FCSTD DOCUMENT  (FreeCAD 1.0R39109 (Git))
Label: Assembly
License: All rights reserved
LicenseURL: https://en.wikipedia.org/wiki/All_rights_reserved
objects: App::FeaturePython×14, App::Link×5, Assembly::JointGroup×1, Assembly::AssemblyObject×1
EXTERNAL_REF file=HalfBridge_SiC.FCStd obj=Board_ed05
EXTERNAL_REF file=Rectifier.FCStd obj=Board_47f8
EXTERNAL_REF file=Backplane_DC.FCStd obj=Board_587c
EXTERNAL_REF file=Filter.FCStd obj=Board_ee73

FEATURE [App::Link] HalfBridge_SiC  label="HalfBridge_SiC1"
  LinkedObject = -> <external HalfBridge_SiC.FCStd>#Board_ed05
FEATURE [App::Link] HalfBridge_SiC001  label="HalfBridge_SiC2"
  LinkPlacement = pos=(-2.33e-14,5.4e-15,60.96) rot=(0,0,1;0rad)
  LinkedObject = -> <external HalfBridge_SiC.FCStd>#Board_ed05
  Placement = pos=(-2.33e-14,5.4e-15,60.96) rot=(0,0,1;0rad)
FEATURE [App::Link] Rectifier
  LinkPlacement = pos=(0.02,-1e-06,91.44) rot=(0,0,1;0rad)
  LinkedObject = -> <external Rectifier.FCStd>#Board_47f8
  Placement = pos=(0.02,-1e-06,91.44) rot=(0,0,1;0rad)
FEATURE [App::FeaturePython] GroundedJoint  # Assembly grounded joint (typed FeaturePython)
  ObjectToGround = -> HalfBridge_SiC
FEATURE [App::FeaturePython] Joint003  label="Parallel001"  # Assembly joint (typed FeaturePython)
  Activated = true
  AngleMax = 0
  AngleMin = 0
  Detach1 = false
  Detach2 = false
  Distance = 0
  Distance2 = 0
  EnableAngleMax = false
  EnableAngleMin = false
  EnableLengthMax = false
  EnableLengthMin = false
  JointType = 6 (Parallel)
  LengthMax = 0
  LengthMin = 0
  Placement1 = pos=(139.5,-40.5,0) rot=(1,0,0;1.5708rad)
  Placement2 = pos=(139.5,-40.5,0) rot=(1,0,0;1.5708rad)
  Reference1 = -> Assembly [HalfBridge_SiC.Board_Geoms_ed05.Pcb_ed05.Face1,HalfBridge_SiC.Board_Geoms_ed05.Pcb_ed05.Vertex3]
  Reference2 = -> Assembly [HalfBridge_SiC001.Board_Geoms_ed05.Pcb_ed05.Face1,HalfBridge_SiC001.Board_Geoms_ed05.Pcb_ed05.Vertex3]
FEATURE [App::Link] Backplane_DC
  LinkPlacement = pos=(101.6,-2e-06,92.078) rot=(0,1,0;1.5708rad)
  LinkedObject = -> <external Backplane_DC.FCStd>#Board_587c
  Placement = pos=(101.6,-2e-06,92.078) rot=(0,1,0;1.5708rad)
FEATURE [App::FeaturePython] Joint  label="Distance"  # Assembly joint (typed FeaturePython)
  Activated = true
  AngleMax = 0
  AngleMin = 0
  Detach1 = false
  Detach2 = false
  Distance = 0
  Distance2 = 0
  EnableAngleMax = false
  EnableAngleMin = false
  EnableLengthMax = false
  EnableLengthMin = false
  JointType = 5 (Distance)
  LengthMax = 0
  LengthMin = 0
  Placement1 = pos=(-1.42e-14,-3.5,2.35667) rot=(0.57735,0.57735,0.57735;4.18879rad)
  Placement2 = pos=(89.9794,-90.1131,-1.6) rot=(0,1,0;3.14159rad)
  Reference1 = -> Assembly [HalfBridge_SiC.Step_Models_ed05.Bot_ed05.J13_1_cfcac89c0bd5_2__ln_001.Face4,HalfBridge_SiC.Step_Models_ed05.Bot_ed05.J13_1_cfcac89c0bd5_2__ln_001.Vertex4]
  Reference2 = -> Assembly [Backplane_DC.Board_Geoms_587c.Pcb_587c.Face27,Backplane_DC.Board_Geoms_587c.Pcb_587c.Face27]
FEATURE [App::FeaturePython] Joint004  label="Cylindrical"  # Assembly joint (typed FeaturePython)
  Activated = true
  AngleMax = 0
  AngleMin = 0
  Detach1 = false
  Detach2 = false
  Distance = 0
  Distance2 = 0
  EnableAngleMax = false
  EnableAngleMin = false
  EnableLengthMax = false
  EnableLengthMin = false
  JointType = 2 (Cylindrical)
  LengthMax = 0
  LengthMin = 0
  Placement1 = pos=(0,-3.13,1.98) rot=(0.57735,0.57735,-0.57735;2.0944rad)
  Placement2 = pos=(135.658,-116.2,-0.8) rot=(0,0,1;0rad)
  Reference1 = -> Assembly [HalfBridge_SiC.Step_Models_ed05.Bot_ed05.J13_1_cfcac89c0bd5_2__ln_001.Face2,HalfBridge_SiC.Step_Models_ed05.Bot_ed05.J13_1_cfcac89c0bd5_2__ln_001.Edge3]
  Reference2 = -> Assembly [Backplane_DC.Board_Geoms_587c.Pcb_587c.Face11,Backplane_DC.Board_Geoms_587c.Pcb_587c.Face11]
FEATURE [App::FeaturePython] Joint005  label="Parallel"  # Assembly joint (typed FeaturePython)
  Activated = true
  AngleMax = 0
  AngleMin = 0
  Detach1 = false
  Detach2 = false
  Distance = 0
  Distance2 = 0
  EnableAngleMax = false
  EnableAngleMin = false
  EnableLengthMax = false
  EnableLengthMin = false
  JointType = 6 (Parallel)
  LengthMax = 0
  LengthMin = 0
  Placement1 = pos=(139.5,-140.5,-1.6) rot=(0,0.707107,0.707107;3.14159rad)
  Placement2 = pos=(140,-140,-1.6) rot=(0,0.707107,0.707107;3.14159rad)
  Reference1 = -> Assembly [HalfBridge_SiC.Board_Geoms_ed05.Pcb_ed05.Face4,HalfBridge_SiC.Board_Geoms_ed05.Pcb_ed05.Vertex8]
  Reference2 = -> Assembly [Backplane_DC.Board_Geoms_587c.Pcb_587c.Face4,Backplane_DC.Board_Geoms_587c.Pcb_587c.Vertex8]
FEATURE [App::FeaturePython] Joint006  label="Distance001"  # Assembly joint (typed FeaturePython)
  Activated = true
  AngleMax = 0
  AngleMin = 0
  Detach1 = false
  Detach2 = false
  Distance = 0
  Distance2 = 0
  EnableAngleMax = false
  EnableAngleMin = false
  EnableLengthMax = false
  EnableLengthMin = false
  JointType = 5 (Distance)
  LengthMax = 0
  LengthMin = 0
  Placement1 = pos=(-1.42e-14,-3.5,2.35667) rot=(0.57735,0.57735,0.57735;4.18879rad)
  Placement2 = pos=(89.9794,-90.1131,-1.6) rot=(0,1,0;3.14159rad)
  Reference1 = -> Assembly [HalfBridge_SiC001.Step_Models_ed05.Bot_ed05.J13_1_cfcac89c0bd5_2__ln_001.Face4,HalfBridge_SiC001.Step_Models_ed05.Bot_ed05.J13_1_cfcac89c0bd5_2__ln_001.Vertex4]
  Reference2 = -> Assembly [Backplane_DC.Board_Geoms_587c.Pcb_587c.Face27,Backplane_DC.Board_Geoms_587c.Pcb_587c.Vertex28]
FEATURE [App::FeaturePython] Joint007  label="Cylindrical001"  # Assembly joint (typed FeaturePython)
  Activated = true
  AngleMax = 0
  AngleMin = 0
  Detach1 = false
  Detach2 = false
  Distance = 0
  Distance2 = 0
  EnableAngleMax = false
  EnableAngleMin = false
  EnableLengthMax = false
  EnableLengthMin = false
  JointType = 2 (Cylindrical)
  LengthMax = 0
  LengthMin = 0
  Placement1 = pos=(0,3.13,1.98) rot=(0.57735,0.57735,-0.57735;2.0944rad)
  Placement2 = pos=(74.698,-116.2,-0.8) rot=(0,0,1;0rad)
  Reference1 = -> Assembly [HalfBridge_SiC001.Step_Models_ed05.Bot_ed05.J13_1_cfcac89c0bd5_2__ln_001.Face2,HalfBridge_SiC001.Step_Models_ed05.Bot_ed05.J13_1_cfcac89c0bd5_2__ln_001.Edge1]
  Reference2 = -> Assembly [Backplane_DC.Board_Geoms_587c.Pcb_587c.Face15,Backplane_DC.Board_Geoms_587c.Pcb_587c.Face15]
FEATURE [App::FeaturePython] Joint008  label="Parallel002"  # Assembly joint (typed FeaturePython)
  Activated = true
  AngleMax = 0
  AngleMin = 0
  Detach1 = false
  Detach2 = false
  Distance = 0
  Distance2 = 0
  EnableAngleMax = false
  EnableAngleMin = false
  EnableLengthMax = false
  EnableLengthMin = false
  JointType = 6 (Parallel)
  LengthMax = 0
  LengthMin = 0
  Placement1 = pos=(139.5,-140.5,-1.6) rot=(0,0.707107,0.707107;3.14159rad)
  Placement2 = pos=(90,-140,-0.8) rot=(0,0.707107,0.707107;3.14159rad)
  Reference1 = -> Assembly [HalfBridge_SiC001.Board_Geoms_ed05.Pcb_ed05.Face4,HalfBridge_SiC001.Board_Geoms_ed05.Pcb_ed05.Vertex8]
  Reference2 = -> Assembly [Backplane_DC.Board_Geoms_587c.Pcb_587c.Face4,Backplane_DC.Board_Geoms_587c.Pcb_587c.Face4]
FEATURE [App::FeaturePython] Joint009  label="Distance002"  # Assembly joint (typed FeaturePython)
  Activated = true
  AngleMax = 0
  AngleMin = 0
  Detach1 = false
  Detach2 = false
  Distance = 0
  Distance2 = 0
  EnableAngleMax = false
  EnableAngleMin = false
  EnableLengthMax = false
  EnableLengthMin = false
  JointType = 5 (Distance)
  LengthMax = 0
  LengthMin = 0
  Placement1 = pos=(-1.42e-14,-3.5,2.35667) rot=(0.57735,0.57735,0.57735;4.18879rad)
  Placement2 = pos=(89.9794,-90.1131,-1.6) rot=(0,1,0;3.14159rad)
  Reference1 = -> Assembly [Rectifier.Step_Models_47f8.Bot_47f8.J3_1_837fcd1c15ac_2__ln_001.Face4,Rectifier.Step_Models_47f8.Bot_47f8.J3_1_837fcd1c15ac_2__ln_001.Vertex7]
  Reference2 = -> Assembly [Backplane_DC.Board_Geoms_587c.Pcb_587c.Face27,Backplane_DC.Board_Geoms_587c.Pcb_587c.Vertex32]
FEATURE [App::FeaturePython] Joint010  label="Cylindrical002"  # Assembly joint (typed FeaturePython)
  Activated = true
  AngleMax = 0
  AngleMin = 0
  Detach1 = false
  Detach2 = false
  Distance = 0
  Distance2 = 0
  EnableAngleMax = false
  EnableAngleMin = false
  EnableLengthMax = false
  EnableLengthMin = false
  JointType = 2 (Cylindrical)
  LengthMax = 0
  LengthMin = 0
  Placement1 = pos=(0,-3.13,1.98) rot=(0.57735,0.57735,-0.57735;2.0944rad)
  Placement2 = pos=(44.218,-75.56,-0.8) rot=(0,0,1;0rad)
  Reference1 = -> Assembly [Rectifier.Step_Models_47f8.Bot_47f8.J3_1_837fcd1c15ac_2__ln_.Face2,Rectifier.Step_Models_47f8.Bot_47f8.J3_1_837fcd1c15ac_2__ln_.Edge3]
  Reference2 = -> Assembly [Backplane_DC.Board_Geoms_587c.Pcb_587c.Face23,Backplane_DC.Board_Geoms_587c.Pcb_587c.Face23]
FEATURE [App::FeaturePython] Joint011  label="Parallel003"  # Assembly joint (typed FeaturePython)
  Activated = true
  AngleMax = 0
  AngleMin = 0
  Detach1 = false
  Detach2 = false
  Distance = 0
  Distance2 = 0
  EnableAngleMax = false
  EnableAngleMin = false
  EnableLengthMax = false
  EnableLengthMin = false
  JointType = 6 (Parallel)
  LengthMax = 0
  LengthMin = 0
  Placement1 = pos=(153.67,-129.248,0) rot=(0,0.707107,0.707107;3.14159rad)
  Placement2 = pos=(40,-140,0) rot=(0,0.707107,0.707107;3.14159rad)
  Reference1 = -> Assembly [Rectifier.Board_Geoms_47f8.Pcb_47f8.Face4,Rectifier.Board_Geoms_47f8.Pcb_47f8.Vertex7]
  Reference2 = -> Assembly [Backplane_DC.Board_Geoms_587c.Pcb_587c.Face4,Backplane_DC.Board_Geoms_587c.Pcb_587c.Vertex5]
FEATURE [App::Link] Filter
  LinkPlacement = pos=(101.6,88.8,-7.922) rot=(1,0,0;1.5708rad)
  LinkedObject = -> <external Filter.FCStd>#Board_ee73
  Placement = pos=(101.6,88.8,-7.922) rot=(1,0,0;1.5708rad)
FEATURE [App::FeaturePython] Joint012  label="Distance003"  # Assembly joint (typed FeaturePython)
  Activated = true
  AngleMax = 0
  AngleMin = 0
  Detach1 = false
  Detach2 = false
  Distance = 0
  Distance2 = 0
  EnableAngleMax = false
  EnableAngleMin = false
  EnableLengthMax = false
  EnableLengthMin = false
  JointType = 5 (Distance)
  LengthMax = 0
  LengthMin = 0
  Placement1 = pos=(-1.42e-14,3.5,2.35667) rot=(0.57735,0.57735,0.57735;4.18879rad)
  Placement2 = pos=(89.9794,-90.1131,0) rot=(0,1,0;3.14159rad)
  Reference1 = -> Assembly [Filter.Step_Models_ee73.Bot_ee73.J2_1_276a3e213de9_2__ln_.Face5,Filter.Step_Models_ee73.Bot_ee73.J2_1_276a3e213de9_2__ln_.Vertex1]
  Reference2 = -> Assembly [Backplane_DC.Board_Geoms_587c.Pcb_587c.Face26,Backplane_DC.Board_Geoms_587c.Pcb_587c.Edge21]
FEATURE [App::FeaturePython] Joint013  label="Cylindrical003"  # Assembly joint (typed FeaturePython)
  Activated = true
  AngleMax = 0
  AngleMin = 0
  Detach1 = false
  Detach2 = false
  Distance = 0
  Distance2 = 0
  EnableAngleMax = false
  EnableAngleMin = false
  EnableLengthMax = false
  EnableLengthMin = false
  JointType = 2 (Cylindrical)
  LengthMax = 0
  LengthMin = 0
  Placement1 = pos=(128.038,-47.62,-0.8) rot=(0,0,1;0rad)
  Placement2 = pos=(1.8e-15,-3.13,1.98) rot=(0.57735,0.57735,-0.57735;2.0944rad)
  Reference1 = -> Assembly [Backplane_DC.Board_Geoms_587c.Pcb_587c.Face21,Backplane_DC.Board_Geoms_587c.Pcb_587c.Face21]
  Reference2 = -> Assembly [Filter.Step_Models_ee73.Bot_ee73.Shape002.Face2,Filter.Step_Models_ee73.Bot_ee73.Shape002.Edge3]
FEATURE [App::FeaturePython] Joint014  label="Parallel004"  # Assembly joint (typed FeaturePython)
  Activated = true
  AngleMax = 0
  AngleMin = 0
  Detach1 = false
  Detach2 = false
  Distance = 0
  Distance2 = 0
  EnableAngleMax = false
  EnableAngleMin = false
  EnableLengthMax = false
  EnableLengthMin = false
  JointType = 6 (Parallel)
  LengthMax = 0
  LengthMin = 0
  Placement1 = pos=(140,-40,0) rot=(0.57735,-0.57735,-0.57735;2.0944rad)
  Placement2 = pos=(40,-160,0) rot=(0,0.707107,0.707107;3.14159rad)
  Reference1 = -> Assembly [Backplane_DC.Board_Geoms_587c.Pcb_587c.Face3,Backplane_DC.Board_Geoms_587c.Pcb_587c.Vertex3]
  Reference2 = -> Assembly [Filter.Board_Geoms_ee73.Pcb_ee73.Face4,Filter.Board_Geoms_ee73.Pcb_ee73.Vertex5]
FEATURE [Assembly::JointGroup] Joints
  Group = -> [GroundedJoint,Joint003,Joint,Joint004,Joint005,Joint006,Joint007,Joint008,Joint009,Joint010,Joint011,Joint012,Joint013,Joint014]
FEATURE [Assembly::AssemblyObject] Assembly
  Group = -> [Joints,HalfBridge_SiC,HalfBridge_SiC001,Rectifier,GroundedJoint,Joint003,Backplane_DC,Joint,Joint004,Joint005,Joint006,Joint007,Joint008,Joint009,Joint010,Joint011,Filter,Joint012,Joint013,Joint014]
  Origin = -> Origin
  Type = Assembly

RESOLVED EXTERNAL PARTS (link-assembly join: the EXTERNAL_REF files above that resolve inside this repo's crawl, each included once):
---- part HalfBridge_SiC.FCStd = doc fcstd_651f331eab62 ----
FCSTD DOCUMENT  (FreeCAD 1.0R39109 (Git))
Label: HalfBridge_SiC
License: All rights reserved
LicenseURL: https://en.wikipedia.org/wiki/All_rights_reserved
objects: App::Link×105, Part::Feature×46, App::Part×15, PartDesign::CoordinateSystem×1, Sketcher::SketchObject×1
note: 49 computed .brp shape members not serialized (recipe doc carries the construction recipe); baked Part::Feature solids carry a one-line shape summary decoded from their .brp

FEATURE [PartDesign::CoordinateSystem] Local_CS_ed05
  AttacherType = Attacher::AttachEngine3D
  MapMode = 2
FEATURE [Part::Feature] Pcb_ed05
  Placement = pos=(-39.5,140.5,0) rot=(0,0,1;0rad)
  shape: bbox 100 x 100 x 1.6 mm, 113 faces (baked)
FEATURE [Sketcher::SketchObject] PCB_Sketch_ed05
  ArcFitTolerance = 1e-06
  FullyConstrained = false
  MakeInternals = false
  sketch-geometry (28):
    g0: LineSegment StartX=17.542 StartY=39.29 StartZ=0 EndX=18.542 EndY=39.29 EndZ=0
    g1: LineSegment StartX=18.542 StartY=39.29 StartZ=0 EndX=18.542 EndY=29.29 EndZ=0
    g2: LineSegment StartX=18.542 StartY=29.29 StartZ=0 EndX=17.542 EndY=29.29 EndZ=0
    g3: LineSegment StartX=17.542 StartY=29.29 StartZ=0 EndX=17.542 EndY=39.29 EndZ=0
    g4: LineSegment StartX=36.399 StartY=40.662 StartZ=0 EndX=45.383 EndY=40.662 EndZ=0
    g5: LineSegment StartX=45.383 StartY=40.662 StartZ=0 EndX=45.383 EndY=39.662 EndZ=0
    g6: LineSegment StartX=45.383 StartY=39.662 StartZ=0 EndX=36.399 EndY=39.662 EndZ=0
    g7: LineSegment StartX=36.399 StartY=39.662 StartZ=0 EndX=36.399 EndY=40.662 EndZ=0
    g8: LineSegment StartX=47.768 StartY=91.487 StartZ=0 EndX=48.514 EndY=91.487 EndZ=0
    g9: LineSegment StartX=48.514 StartY=91.487 StartZ=0 EndX=48.514 EndY=59.389 EndZ=0
    g10: LineSegment StartX=48.514 StartY=59.389 StartZ=0 EndX=47.768 EndY=59.389 EndZ=0
    g11: LineSegment StartX=47.768 StartY=59.389 StartZ=0 EndX=47.768 EndY=91.487 EndZ=0
    g12: LineSegment StartX=17.968 StartY=23.7 StartZ=0 EndX=74.68 EndY=23.7 EndZ=0
    g13: LineSegment StartX=74.68 StartY=23.7 StartZ=0 EndX=74.68 EndY=22.7 EndZ=0
    g14: LineSegment StartX=74.68 StartY=22.7 StartZ=0 EndX=17.968 EndY=22.7 EndZ=0
    g15: LineSegment StartX=17.968 StartY=22.7 StartZ=0 EndX=17.968 EndY=23.7 EndZ=0
    g16: LineSegment StartX=0 StartY=100 StartZ=0 EndX=100 EndY=100 EndZ=0
    g17: LineSegment StartX=100 StartY=100 StartZ=0 EndX=100 EndY=0 EndZ=0
    g18: LineSegment StartX=100 StartY=0 StartZ=0 EndX=0 EndY=0 EndZ=0
    g19: LineSegment StartX=0 StartY=0 StartZ=0 EndX=0 EndY=100 EndZ=0
    g20: LineSegment StartX=18.05 StartY=15.208 StartZ=0 EndX=19.05 EndY=15.208 EndZ=0
    g21: LineSegment StartX=19.05 StartY=15.208 StartZ=0 EndX=19.05 EndY=8.7 EndZ=0
    g22: LineSegment StartX=19.05 StartY=8.7 StartZ=0 EndX=18.05 EndY=8.7 EndZ=0
    g23: LineSegment StartX=18.05 StartY=8.7 StartZ=0 EndX=18.05 EndY=15.208 EndZ=0
    g24: LineSegment StartX=15.764 StartY=29.4 StartZ=0 EndX=16.764 EndY=29.4 EndZ=0
    g25: LineSegment StartX=16.764 StartY=29.4 StartZ=0 EndX=16.764 EndY=16.9 EndZ=0
    g26: LineSegment StartX=16.764 StartY=16.9 StartZ=0 EndX=15.764 EndY=16.9 EndZ=0
    g27: LineSegment StartX=15.764 StartY=16.9 StartZ=0 EndX=15.764 EndY=29.4 EndZ=0
  constraints (28):
    c: Coincident(g18,g19)
    c: Coincident(g16,g19)
    c: Coincident(g26,g27)
    c: Coincident(g24,g27)
    c: Coincident(g25,g26)
    c: Coincident(g24,g25)
    c: Coincident(g2,g3)
    c: Coincident(g0,g3)
    c: Coincident(g14,g15)
    c: Coincident(g12,g15)
    c: Coincident(g22,g23)
    c: Coincident(g20,g23)
    c: Coincident(g1,g2)
    c: Coincident(g0,g1)
    c: Coincident(g21,g22)
    c: Coincident(g20,g21)
    c: Coincident(g6,g7)
    c: Coincident(g4,g7)
    c: Coincident(g5,g6)
    c: Coincident(g4,g5)
    c: Coincident(g10,g11)
    c: Coincident(g8,g11)
    c: Coincident(g9,g10)
    c: Coincident(g8,g9)
    c: Coincident(g13,g14)
    c: Coincident(g12,g13)
    c: Coincident(g17,g18)
    c: Coincident(g16,g17)
FEATURE [App::Part] Board_Geoms_ed05
  Group = -> [Pcb_ed05,PCB_Sketch_ed05]
  Origin = -> Origin
FEATURE [Part::Feature] Shape  label="U5_SOIC-16W_7.5x10.3mm_P1.27mm_noPin12_13_606f1c37d418"
  Placement = pos=(18,23.3,0) rot=(0,0,1;0rad)
  shape: bbox 10.3 x 10.3 x 2.75 mm, 256 faces (baked)
FEATURE [Part::Feature] Shape001  label="D6_D_SOD_123_86f777a7cf57"
  Placement = pos=(31.3,17.35,0) rot=(0,0,-1;1.5708rad)
  shape: bbox 1.6 x 3.8 x 1.25 mm, 67 faces (baked)
FEATURE [Part::Feature] Shape002  label="R9_R_0603_1608Metric_fe9d9f34c5f9"
  Placement = pos=(9.9875,27.2,0) rot=(0,0,1;0rad)
  shape: bbox 1.6 x 0.8 x 0.45 mm, 26 faces (baked)
FEATURE [App::Link] D6_D_SOD_123_86f777a7cf57_ln_  label="D5_D_SOD_123_75c73be4f775"
  LinkPlacement = pos=(31.3,29.9,0) rot=(0,0,1;1.5708rad)
  LinkedObject = -> Shape001
  Placement = pos=(31.3,29.9,0) rot=(0,0,1;1.5708rad)
FEATURE [Part::Feature] Shape003  label="C15_C_0603_1608Metric_09ddd0478757"
  Placement = pos=(13.5,16.1,0) rot=(0,0,-1;1.5708rad)
  shape: bbox 0.8 x 1.6 x 0.8 mm, 28 faces (baked)
FEATURE [App::Link] C15_C_0603_1608Metric_09ddd0478757_ln_  label="C33_C_0603_1608Metric_74bc470caa33"
  LinkPlacement = pos=(9.3,80.8715,0) rot=(0,0,1;1.5708rad)
  LinkedObject = -> Shape003
  Placement = pos=(9.3,80.8715,0) rot=(0,0,1;1.5708rad)
FEATURE [Part::Feature] Shape004  label="D3_LED_0603_1608Metric_70bb5031e2ff"
  Placement = pos=(4.7,31.775,0) rot=(0,0,-1;1.5708rad)
  shape: bbox 0.8 x 1.6 x 1.1 mm, 50 faces (baked)
FEATURE [Part::Feature] Shape005  label="C38_C_0805_2012Metric_74cbd35bff10"
  Placement = pos=(6.655,73.284,0) rot=(0,0,1;0rad)
  shape: bbox 2 x 1.25 x 1.25 mm, 28 faces (baked)
FEATURE [App::Link] R9_R_0603_1608Metric_fe9d9f34c5f9_ln_  label="R33_R_0603_1608Metric_ea8747869db3"
  LinkPlacement = pos=(22.7,83.4115,0) rot=(0,0,1;1.5708rad)
  LinkedObject = -> Shape002
  Placement = pos=(22.7,83.4115,0) rot=(0,0,1;1.5708rad)
FEATURE [App::Link] C15_C_0603_1608Metric_09ddd0478757_ln_001  label="C22_C_0603_1608Metric_3b7886544036"
  LinkPlacement = pos=(25.65,28.3,0) rot=(0,0,1;0rad)
  LinkedObject = -> Shape003
  Placement = pos=(25.65,28.3,0) rot=(0,0,1;0rad)
FEATURE [Part::Feature] Part__Feature  label="CAS_c_12B"
  Placement = pos=(0,-2.4,-3e-16) rot=(0,0,1;0rad)
  shape: bbox 5.4 x 2.5 x 4.2 mm, 71 faces (baked)
FEATURE [Part::Feature] Part__Feature001  label="1 pole_s"
  Placement = pos=(0.3,-0.6,-3e-16) rot=(0,0,1;0rad)
  shape: bbox 0.6 x 0.6 x 0.7 mm, 14 faces (baked)
FEATURE [App::Part] CAS_120B1  label="SW1_CAS-120B1_eba1f44a47b7[2]"
  Group = -> [Part__Feature,Part__Feature001]
  Origin = -> Origin008
  Placement = pos=(29.242,83.058,2.5) rot=(0.57735,-0.57735,-0.57735;2.0944rad)
FEATURE [App::Link] R9_R_0603_1608Metric_fe9d9f34c5f9_ln_001  label="R14_R_0603_1608Metric_f9b5c031c635"
  LinkPlacement = pos=(28.1,36.5,0) rot=(0,0,1;1.5708rad)
  LinkedObject = -> Shape002
  Placement = pos=(28.1,36.5,0) rot=(0,0,1;1.5708rad)
FEATURE [App::Link] R9_R_0603_1608Metric_fe9d9f34c5f9_ln_002  label="R8_R_0603_1608Metric_fcb6b5fbbfd0"
  LinkPlacement = pos=(10,28.7,0) rot=(0,0,1;0rad)
  LinkedObject = -> Shape002
  Placement = pos=(10,28.7,0) rot=(0,0,1;0rad)
FEATURE [App::Link] C15_C_0603_1608Metric_09ddd0478757_ln_002  label="C45_C_0603_1608Metric_6c9f5762c5a1"
  LinkPlacement = pos=(36.9,16.256,0) rot=(0,0,1;1.5708rad)
  LinkedObject = -> Shape003
  Placement = pos=(36.9,16.256,0) rot=(0,0,1;1.5708rad)
FEATURE [App::Link] C38_C_0805_2012Metric_74cbd35bff10_ln_  label="C24_C_0805_2012Metric_4c91d95a9eef"
  LinkPlacement = pos=(25.7,8.7,0) rot=(0,0,1;3.14159rad)
  LinkedObject = -> Shape005
  Placement = pos=(25.7,8.7,0) rot=(0,0,1;3.14159rad)
FEATURE [Part::Feature] Shape006  label="U10_SOT_23_6_8cf1dc40b667"
  Placement = pos=(21.85,68.3115,0) rot=(0,0,1;3.14159rad)
  shape: bbox 2.8 x 2.9 x 1.55 mm, 124 faces (baked)
FEATURE [App::Link] C15_C_0603_1608Metric_09ddd0478757_ln_003  label="C21_C_0603_1608Metric_d16c1e161e8d"
  LinkPlacement = pos=(25.62,18.5,0) rot=(0,0,1;3.14159rad)
  LinkedObject = -> Shape003
  Placement = pos=(25.62,18.5,0) rot=(0,0,1;3.14159rad)
FEATURE [App::Link] C15_C_0603_1608Metric_09ddd0478757_ln_004  label="C42_C_0603_1608Metric_20bf4b114d9d"
  LinkPlacement = pos=(25.1,68.1115,0) rot=(0,0,1;1.5708rad)
  LinkedObject = -> Shape003
  Placement = pos=(25.1,68.1115,0) rot=(0,0,1;1.5708rad)
FEATURE [App::Link] C38_C_0805_2012Metric_74cbd35bff10_ln_001  label="C18_C_0805_2012Metric_4df3bd6c3c50"
  LinkPlacement = pos=(25.7,33.1,0) rot=(0,0,1;3.14159rad)
  LinkedObject = -> Shape005
  Placement = pos=(25.7,33.1,0) rot=(0,0,1;3.14159rad)
FEATURE [App::Link] U10_SOT_23_6_8cf1dc40b667_ln_  label="U11_SOT_23_6_c211cb7acc4a"
  LinkPlacement = pos=(21.85,58.1515,0) rot=(0,0,1;3.14159rad)
  LinkedObject = -> Shape006
  Placement = pos=(21.85,58.1515,0) rot=(0,0,1;3.14159rad)
FEATURE [App::Link] R9_R_0603_1608Metric_fe9d9f34c5f9_ln_003  label="R15_R_0603_1608Metric_55e85660f00f"
  LinkPlacement = pos=(22.6,36.1,0) rot=(0,0,-1;1.5708rad)
  LinkedObject = -> Shape002
  Placement = pos=(22.6,36.1,0) rot=(0,0,-1;1.5708rad)
FEATURE [Part::Feature] Shape007  label="R21_R_0805_2012Metric_4eff570911b6"
  Placement = pos=(34.3,28.2,0) rot=(0,0,1;0rad)
  shape: bbox 2 x 1.2 x 0.45 mm, 26 faces (baked)
FEATURE [App::Link] C15_C_0603_1608Metric_09ddd0478757_ln_005  label="C34_C_0603_1608Metric_836b7f75df63"
  LinkPlacement = pos=(9.5,60.3715,0) rot=(0,0,1;1.5708rad)
  LinkedObject = -> Shape003
  Placement = pos=(9.5,60.3715,0) rot=(0,0,1;1.5708rad)
FEATURE [App::Link] C38_C_0805_2012Metric_74cbd35bff10_ln_002  label="C39_C_0805_2012Metric_4739b33e3560"
  LinkPlacement = pos=(6.655,83.9115,0) rot=(0,0,1;0rad)
  LinkedObject = -> Shape005
  Placement = pos=(6.655,83.9115,0) rot=(0,0,1;0rad)
FEATURE [App::Link] R9_R_0603_1608Metric_fe9d9f34c5f9_ln_004  label="R16_R_0603_1608Metric_5e29ad9bbd6c"
  LinkPlacement = pos=(29.7,13.3,0) rot=(0,0,-1;1.5708rad)
  LinkedObject = -> Shape002
  Placement = pos=(29.7,13.3,0) rot=(0,0,-1;1.5708rad)
FEATURE [App::Link] C15_C_0603_1608Metric_09ddd0478757_ln_006  label="C6_C_0603_1608Metric_47ec0beeeb7c"
  LinkPlacement = pos=(36.576,85.598,0) rot=(0,0,1;0rad)
  LinkedObject = -> Shape003
  Placement = pos=(36.576,85.598,0) rot=(0,0,1;0rad)
FEATURE [App::Link] D3_LED_0603_1608Metric_70bb5031e2ff_ln_  label="D1_LED_0603_1608Metric_117d22e4d741"
  LinkPlacement = pos=(3.1,9.525,0) rot=(0,0,1;1.5708rad)
  LinkedObject = -> Shape004
  Placement = pos=(3.1,9.525,0) rot=(0,0,1;1.5708rad)
FEATURE [Part::Feature] Shape008  label="U3_SOT_23_5_e32904241429"
  Placement = pos=(34.37,62.7015,0) rot=(0,0,1;0rad)
  shape: bbox 2.8 x 2.9 x 1.55 mm, 109 faces (baked)
FEATURE [App::Link] C38_C_0805_2012Metric_74cbd35bff10_ln_003  label="C35_C_0805_2012Metric_12818f10c88b"
  LinkPlacement = pos=(7.5,67.9115,0) rot=(0,0,1;3.14159rad)
  LinkedObject = -> Shape005
  Placement = pos=(7.5,67.9115,0) rot=(0,0,1;3.14159rad)
FEATURE [Part::Feature] Shape009  label="U7_SOT_23_ed8fd63cd947"
  Placement = pos=(25.3625,36.5,0) rot=(0,0,1;3.14159rad)
  shape: bbox 2.5 x 3 x 1.2 mm, 76 faces (baked)
FEATURE [Part::Feature] Shape010  label="C5_C_2220_5750Metric_40789e461117"
  Placement = pos=(71.498,23.622,0) rot=(0,0,-1;1.5708rad)
  shape: bbox 5 x 5.7 x 2.9 mm, 28 faces (baked)
FEATURE [App::Link] R9_R_0603_1608Metric_fe9d9f34c5f9_ln_005  label="R29_R_0603_1608Metric_c415b56a8a35"
  LinkPlacement = pos=(13.655,63.4115,0) rot=(0,0,1;1.5708rad)
  LinkedObject = -> Shape002
  Placement = pos=(13.655,63.4115,0) rot=(0,0,1;1.5708rad)
FEATURE [App::Link] R9_R_0603_1608Metric_fe9d9f34c5f9_ln_006  label="R27_R_0603_1608Metric_6ecdd8c441b3"
  LinkPlacement = pos=(13.3,73.9115,0) rot=(0,0,1;1.5708rad)
  LinkedObject = -> Shape002
  Placement = pos=(13.3,73.9115,0) rot=(0,0,1;1.5708rad)
FEATURE [App::Link] R9_R_0603_1608Metric_fe9d9f34c5f9_ln_007  label="R30_R_0603_1608Metric_3d9fcfb98980"
  LinkPlacement = pos=(18.7,78.4115,0) rot=(0,0,1;1.5708rad)
  LinkedObject = -> Shape002
  Placement = pos=(18.7,78.4115,0) rot=(0,0,1;1.5708rad)
FEATURE [App::Link] C15_C_0603_1608Metric_09ddd0478757_ln_007  label="C41_C_0603_1608Metric_8a3fc6cb6ce4"
  LinkPlacement = pos=(25.1,78.4115,0) rot=(0,0,1;1.5708rad)
  LinkedObject = -> Shape003
  Placement = pos=(25.1,78.4115,0) rot=(0,0,1;1.5708rad)
FEATURE [App::Link] C5_C_2220_5750Metric_40789e461117_ln_  label="C3_C_2220_5750Metric_0b14797a19db"
  LinkPlacement = pos=(59.498,23.622,0) rot=(0,0,-1;1.5708rad)
  LinkedObject = -> Shape010
  Placement = pos=(59.498,23.622,0) rot=(0,0,-1;1.5708rad)
FEATURE [App::Link] R21_R_0805_2012Metric_4eff570911b6_ln_  label="R19_R_0805_2012Metric_5467f9f4486e"
  LinkPlacement = pos=(34.3,32.2,0) rot=(0,0,1;0rad)
  LinkedObject = -> Shape007
  Placement = pos=(34.3,32.2,0) rot=(0,0,1;0rad)
FEATURE [App::Link] C15_C_0603_1608Metric_09ddd0478757_ln_008  label="C43_C_0603_1608Metric_b35c248b52c4"
  LinkPlacement = pos=(25.1,58.1115,0) rot=(0,0,1;1.5708rad)
  LinkedObject = -> Shape003
  Placement = pos=(25.1,58.1115,0) rot=(0,0,1;1.5708rad)
FEATURE [App::Link] R21_R_0805_2012Metric_4eff570911b6_ln_001  label="R3_R_0805_2012Metric_ab16afa742b3"
  LinkPlacement = pos=(44.564,16.278,0) rot=(0,0,1;1.5708rad)
  LinkedObject = -> Shape007
  Placement = pos=(44.564,16.278,0) rot=(0,0,1;1.5708rad)
FEATURE [App::Link] R21_R_0805_2012Metric_4eff570911b6_ln_002  label="R10_R_0805_2012Metric_e1b373d5c9e0"
  LinkPlacement = pos=(8.1,18.67,0) rot=(0,0,-1;1.5708rad)
  LinkedObject = -> Shape007
  Placement = pos=(8.1,18.67,0) rot=(0,0,-1;1.5708rad)
FEATURE [App::Link] D3_LED_0603_1608Metric_70bb5031e2ff_ln_001  label="D2_LED_0603_1608Metric_72f350e39bfe"
  LinkPlacement = pos=(4.7,35.5,0) rot=(0,0,-1;1.5708rad)
  LinkedObject = -> Shape004
  Placement = pos=(4.7,35.5,0) rot=(0,0,-1;1.5708rad)
FEATURE [App::Link] R9_R_0603_1608Metric_fe9d9f34c5f9_ln_008  label="R32_R_0603_1608Metric_bd0168379d35"
  LinkPlacement = pos=(18.7,58.1115,0) rot=(0,0,1;1.5708rad)
  LinkedObject = -> Shape002
  Placement = pos=(18.7,58.1115,0) rot=(0,0,1;1.5708rad)
FEATURE [App::Link] C38_C_0805_2012Metric_74cbd35bff10_ln_004  label="C40_C_0805_2012Metric_1a8242036e69"
  LinkPlacement = pos=(6.7,63.1115,0) rot=(0,0,1;0rad)
  LinkedObject = -> Shape005
  Placement = pos=(6.7,63.1115,0) rot=(0,0,1;0rad)
FEATURE [App::Link] R21_R_0805_2012Metric_4eff570911b6_ln_003  label="R40_R_0805_2012Metric_1fb8d6502ab2"
  LinkPlacement = pos=(20.574,16.04,0) rot=(0,0,-1;1.5708rad)
  LinkedObject = -> Shape007
  Placement = pos=(20.574,16.04,0) rot=(0,0,-1;1.5708rad)
FEATURE [App::Link] C15_C_0603_1608Metric_09ddd0478757_ln_009  label="C20_C_0603_1608Metric_5de1c2e82c4e"
  LinkPlacement = pos=(25.62,21.1,0) rot=(0,0,1;0rad)
  LinkedObject = -> Shape003
  Placement = pos=(25.62,21.1,0) rot=(0,0,1;0rad)
FEATURE [App::Link] R9_R_0603_1608Metric_fe9d9f34c5f9_ln_009  label="R28_R_0603_1608Metric_db2da8ac741f"
  LinkPlacement = pos=(13.3,84.0715,0) rot=(0,0,1;1.5708rad)
  LinkedObject = -> Shape002
  Placement = pos=(13.3,84.0715,0) rot=(0,0,1;1.5708rad)
FEATURE [App::Link] C38_C_0805_2012Metric_74cbd35bff10_ln_005  label="C25_C_0805_2012Metric_d4570dd2b406"
  LinkPlacement = pos=(21.9,8.7,0) rot=(0,0,1;3.14159rad)
  LinkedObject = -> Shape005
  Placement = pos=(21.9,8.7,0) rot=(0,0,1;3.14159rad)
FEATURE [Part::Feature] Shape011  label="L5_L_0603_1608Metric_90973c27a168"
  Placement = pos=(5.1,81.1115,0) rot=(0,0,1;1.5708rad)
  shape: bbox 0.8 x 1.6 x 0.8 mm, 28 faces (baked)
FEATURE [App::Link] R21_R_0805_2012Metric_4eff570911b6_ln_004  label="R26_R_0805_2012Metric_215f856b24f5"
  LinkPlacement = pos=(34.3,13.9,0) rot=(0,0,1;0rad)
  LinkedObject = -> Shape007
  Placement = pos=(34.3,13.9,0) rot=(0,0,1;0rad)
FEATURE [App::Link] L5_L_0603_1608Metric_90973c27a168_ln_  label="L6_L_0603_1608Metric_227bb48d5cae"
  LinkPlacement = pos=(5.1,60.4265,0) rot=(0,0,1;1.5708rad)
  LinkedObject = -> Shape011
  Placement = pos=(5.1,60.4265,0) rot=(0,0,1;1.5708rad)
FEATURE [App::Link] C15_C_0603_1608Metric_09ddd0478757_ln_010  label="C14_C_0603_1608Metric_a25fa12fbfe8"
  LinkPlacement = pos=(11.3,24.6,0) rot=(0,0,-1;1.5708rad)
  LinkedObject = -> Shape003
  Placement = pos=(11.3,24.6,0) rot=(0,0,-1;1.5708rad)
FEATURE [App::Link] R9_R_0603_1608Metric_fe9d9f34c5f9_ln_010  label="R31_R_0603_1608Metric_1647f0dc400e"
  LinkPlacement = pos=(18.7,68.3115,0) rot=(0,0,1;1.5708rad)
  LinkedObject = -> Shape002
  Placement = pos=(18.7,68.3115,0) rot=(0,0,1;1.5708rad)
FEATURE [App::Link] C38_C_0805_2012Metric_74cbd35bff10_ln_006  label="C37_C_0805_2012Metric_821d07cd279f"
  LinkPlacement = pos=(7.5,57.7115,0) rot=(0,0,1;3.14159rad)
  LinkedObject = -> Shape005
  Placement = pos=(7.5,57.7115,0) rot=(0,0,1;3.14159rad)
FEATURE [App::Link] C5_C_2220_5750Metric_40789e461117_ln_001  label="C4_C_2220_5750Metric_aeb9c5b40f04"
  LinkPlacement = pos=(65.498,23.622,0) rot=(0,0,-1;1.5708rad)
  LinkedObject = -> Shape010
  Placement = pos=(65.498,23.622,0) rot=(0,0,-1;1.5708rad)
FEATURE [Part::Feature] Part__Feature002  label="CAS_c_D2B"
  Placement = pos=(0,-2.4,-3e-16) rot=(0,0,1;0rad)
  shape: bbox 5.4 x 2.5 x 5.6 mm, 110 faces (baked)
FEATURE [Part::Feature] Part__Feature003  label="Dual_s"
  Placement = pos=(0.3,-0.6,0.64) rot=(0,0,1;0rad)
  shape: bbox 0.6 x 0.6 x 0.7 mm, 14 faces (baked)
FEATURE [Part::Feature] Part__Feature004  label="Dual_s001"
  Placement = pos=(0.3,-0.6,-0.64) rot=(0,0,1;0rad)
  shape: bbox 0.6 x 0.6 x 0.7 mm, 14 faces (baked)
FEATURE [App::Part] CAS_D20B1  label="SW5_CAS-D20B1_b4c165cab9b4[2]"
  Group = -> [Part__Feature002,Part__Feature003,Part__Feature004]
  Origin = -> Origin009
  Placement = pos=(4.29,22.754,2.5) rot=(0,0.707107,0.707107;3.14159rad)
FEATURE [App::Link] R9_R_0603_1608Metric_fe9d9f34c5f9_ln_011  label="R35_R_0603_1608Metric_3c432ada0ca8"
  LinkPlacement = pos=(22.7,72.9115,0) rot=(0,0,1;1.5708rad)
  LinkedObject = -> Shape002
  Placement = pos=(22.7,72.9115,0) rot=(0,0,1;1.5708rad)
FEATURE [App::Link] U7_SOT_23_ed8fd63cd947_ln_  label="U8_SOT_23_df60fcb6f98c"
  LinkPlacement = pos=(25.3625,13.6,0) rot=(0,0,1;3.14159rad)
  LinkedObject = -> Shape009
  Placement = pos=(25.3625,13.6,0) rot=(0,0,1;3.14159rad)
FEATURE [App::Link] L5_L_0603_1608Metric_90973c27a168_ln_001  label="L4_L_0603_1608Metric_8fa15f76ae30"
  LinkPlacement = pos=(5.1,70.5865,0) rot=(0,0,1;1.5708rad)
  LinkedObject = -> Shape011
  Placement = pos=(5.1,70.5865,0) rot=(0,0,1;1.5708rad)
FEATURE [App::Link] SW1_CAS_120B1_eba1f44a47b7_2__ln_  label="SW3_CAS-120B1_d768a4589788[2]"
  LinkPlacement = pos=(29.21,62.484,2.5) rot=(0.57735,-0.57735,-0.57735;2.0944rad)
  LinkedObject = -> CAS_120B1
  Placement = pos=(29.21,62.484,2.5) rot=(0.57735,-0.57735,-0.57735;2.0944rad)
FEATURE [App::Link] C15_C_0603_1608Metric_09ddd0478757_ln_011  label="C32_C_0603_1608Metric_89b2b6ef811b"
  LinkPlacement = pos=(9.3,70.7115,0) rot=(0,0,1;1.5708rad)
  LinkedObject = -> Shape003
  Placement = pos=(9.3,70.7115,0) rot=(0,0,1;1.5708rad)
FEATURE [App::Link] C38_C_0805_2012Metric_74cbd35bff10_ln_007  label="C36_C_0805_2012Metric_4e65c6641553"
  LinkPlacement = pos=(7.9,78.1115,0) rot=(0,0,1;3.14159rad)
  LinkedObject = -> Shape005
  Placement = pos=(7.9,78.1115,0) rot=(0,0,1;3.14159rad)
FEATURE [App::Link] C5_C_2220_5750Metric_40789e461117_ln_002  label="C2_C_2220_5750Metric_dfcbf9cf85c4"
  LinkPlacement = pos=(53.498,23.622,0) rot=(0,0,-1;1.5708rad)
  LinkedObject = -> Shape010
  Placement = pos=(53.498,23.622,0) rot=(0,0,-1;1.5708rad)
FEATURE [App::Link] C15_C_0603_1608Metric_09ddd0478757_ln_012  label="C23_C_0603_1608Metric_094c659e187e"
  LinkPlacement = pos=(25.65,25.3,0) rot=(0,0,1;3.14159rad)
  LinkedObject = -> Shape003
  Placement = pos=(25.65,25.3,0) rot=(0,0,1;3.14159rad)
FEATURE [App::Link] R21_R_0805_2012Metric_4eff570911b6_ln_005  label="R20_R_0805_2012Metric_ea78c8c8eecd"
  LinkPlacement = pos=(34.3,30.2,0) rot=(0,0,1;0rad)
  LinkedObject = -> Shape007
  Placement = pos=(34.3,30.2,0) rot=(0,0,1;0rad)
FEATURE [App::Link] C38_C_0805_2012Metric_74cbd35bff10_ln_008  label="C16_C_0805_2012Metric_e5af641f3413"
  LinkPlacement = pos=(12.5,33.7,0) rot=(0,0,1;0rad)
  LinkedObject = -> Shape005
  Placement = pos=(12.5,33.7,0) rot=(0,0,1;0rad)
FEATURE [App::Link] R9_R_0603_1608Metric_fe9d9f34c5f9_ln_012  label="R34_R_0603_1608Metric_211ac095cb09"
  LinkPlacement = pos=(22.7,63.1115,0) rot=(0,0,1;1.5708rad)
  LinkedObject = -> Shape002
  Placement = pos=(22.7,63.1115,0) rot=(0,0,1;1.5708rad)
FEATURE [App::Link] C15_C_0603_1608Metric_09ddd0478757_ln_013  label="C27_C_0603_1608Metric_298082643862"
  LinkPlacement = pos=(23.6375,16.1,0) rot=(0,0,1;3.14159rad)
  LinkedObject = -> Shape003
  Placement = pos=(23.6375,16.1,0) rot=(0,0,1;3.14159rad)
FEATURE [App::Link] R21_R_0805_2012Metric_4eff570911b6_ln_006  label="R2_R_0805_2012Metric_96e20fc01cb7"
  LinkPlacement = pos=(44.564,33.296,0) rot=(0,0,1;1.5708rad)
  LinkedObject = -> Shape007
  Placement = pos=(44.564,33.296,0) rot=(0,0,1;1.5708rad)
FEATURE [App::Link] R9_R_0603_1608Metric_fe9d9f34c5f9_ln_013  label="R13_R_0603_1608Metric_df329fa1d19c"
  LinkPlacement = pos=(29.7,36.5,0) rot=(0,0,-1;1.5708rad)
  LinkedObject = -> Shape002
  Placement = pos=(29.7,36.5,0) rot=(0,0,-1;1.5708rad)
FEATURE [App::Link] U3_SOT_23_5_e32904241429_ln_  label="U2_SOT_23_5_6f2eb00efaad"
  LinkPlacement = pos=(34.37,72.8615,0) rot=(0,0,1;0rad)
  LinkedObject = -> Shape008
  Placement = pos=(34.37,72.8615,0) rot=(0,0,1;0rad)
FEATURE [App::Link] L5_L_0603_1608Metric_90973c27a168_ln_002  label="L2_L_0603_1608Metric_6584b5c4d191"
  LinkPlacement = pos=(9.3,33.1,0) rot=(0,0,-1;1.5708rad)
  LinkedObject = -> Shape011
  Placement = pos=(9.3,33.1,0) rot=(0,0,-1;1.5708rad)
FEATURE [App::Link] L5_L_0603_1608Metric_90973c27a168_ln_003  label="L3_L_0603_1608Metric_80e3bdf1ad67"
  LinkPlacement = pos=(9.3,8.7,0) rot=(0,0,1;1.5708rad)
  LinkedObject = -> Shape011
  Placement = pos=(9.3,8.7,0) rot=(0,0,1;1.5708rad)
FEATURE [App::Link] R21_R_0805_2012Metric_4eff570911b6_ln_007  label="R23_R_0805_2012Metric_772e2aabec3d"
  LinkPlacement = pos=(34.3,19.85,0) rot=(0,0,1;0rad)
  LinkedObject = -> Shape007
  Placement = pos=(34.3,19.85,0) rot=(0,0,1;0rad)
FEATURE [App::Link] C38_C_0805_2012Metric_74cbd35bff10_ln_009  label="C17_C_0805_2012Metric_9d67934c64c5"
  LinkPlacement = pos=(12.1,8.1,0) rot=(0,0,1;0rad)
  LinkedObject = -> Shape005
  Placement = pos=(12.1,8.1,0) rot=(0,0,1;0rad)
FEATURE [App::Link] U10_SOT_23_6_8cf1dc40b667_ln_001  label="U9_SOT_23_6_77935cb89beb"
  LinkPlacement = pos=(21.85,78.4715,0) rot=(0,0,1;3.14159rad)
  LinkedObject = -> Shape006
  Placement = pos=(21.85,78.4715,0) rot=(0,0,1;3.14159rad)
FEATURE [App::Link] C38_C_0805_2012Metric_74cbd35bff10_ln_010  label="C19_C_0805_2012Metric_f233b5c27be5"
  LinkPlacement = pos=(21.9,33.1,0) rot=(0,0,1;3.14159rad)
  LinkedObject = -> Shape005
  Placement = pos=(21.9,33.1,0) rot=(0,0,1;3.14159rad)
FEATURE [App::Link] SW1_CAS_120B1_eba1f44a47b7_2__ln_001  label="SW2_CAS-120B1_de4e8c04cc20[2]"
  LinkPlacement = pos=(29.242,72.898,2.5) rot=(0.57735,-0.57735,-0.57735;2.0944rad)
  LinkedObject = -> CAS_120B1
  Placement = pos=(29.242,72.898,2.5) rot=(0.57735,-0.57735,-0.57735;2.0944rad)
FEATURE [App::Link] R21_R_0805_2012Metric_4eff570911b6_ln_008  label="R25_R_0805_2012Metric_61226d1b2b79"
  LinkPlacement = pos=(34.3,15.9,0) rot=(0,0,1;0rad)
  LinkedObject = -> Shape007
  Placement = pos=(34.3,15.9,0) rot=(0,0,1;0rad)
FEATURE [App::Link] C15_C_0603_1608Metric_09ddd0478757_ln_014  label="C8_C_0603_1608Metric_fd007361b396"
  LinkPlacement = pos=(36.322,65.278,0) rot=(0,0,1;0rad)
  LinkedObject = -> Shape003
  Placement = pos=(36.322,65.278,0) rot=(0,0,1;0rad)
FEATURE [App::Link] C15_C_0603_1608Metric_09ddd0478757_ln_015  label="C7_C_0603_1608Metric_2aaeb20b4386"
  LinkPlacement = pos=(36.4755,75.438,0) rot=(0,0,1;0rad)
  LinkedObject = -> Shape003
  Placement = pos=(36.4755,75.438,0) rot=(0,0,1;0rad)
FEATURE [App::Link] C15_C_0603_1608Metric_09ddd0478757_ln_016  label="C26_C_0603_1608Metric_365ecaa62ea9"
  LinkPlacement = pos=(23.7,38.95,0) rot=(0,0,1;3.14159rad)
  LinkedObject = -> Shape003
  Placement = pos=(23.7,38.95,0) rot=(0,0,1;3.14159rad)
FEATURE [App::Link] C15_C_0603_1608Metric_09ddd0478757_ln_017  label="C11_C_0603_1608Metric_54b4a60d9175"
  LinkPlacement = pos=(10.2875,21.3,0) rot=(0,0,1;3.14159rad)
  LinkedObject = -> Shape003
  Placement = pos=(10.2875,21.3,0) rot=(0,0,1;3.14159rad)
FEATURE [App::Link] R21_R_0805_2012Metric_4eff570911b6_ln_009  label="R24_R_0805_2012Metric_5be639e06338"
  LinkPlacement = pos=(34.3,17.9,0) rot=(0,0,1;0rad)
  LinkedObject = -> Shape007
  Placement = pos=(34.3,17.9,0) rot=(0,0,1;0rad)
FEATURE [App::Link] SW5_CAS_D20B1_b4c165cab9b4_2__ln_  label="SW4_CAS-D20B1_eed64a9be6db[2]"
  LinkPlacement = pos=(4.29,15.168,2.5) rot=(0,0.707107,0.707107;3.14159rad)
  LinkedObject = -> CAS_D20B1
  Placement = pos=(4.29,15.168,2.5) rot=(0,0.707107,0.707107;3.14159rad)
FEATURE [App::Link] R9_R_0603_1608Metric_fe9d9f34c5f9_ln_014  label="R17_R_0603_1608Metric_026225098221"
  LinkPlacement = pos=(28.1,13.3,0) rot=(0,0,1;1.5708rad)
  LinkedObject = -> Shape002
  Placement = pos=(28.1,13.3,0) rot=(0,0,1;1.5708rad)
FEATURE [App::Link] D3_LED_0603_1608Metric_70bb5031e2ff_ln_002  label="D4_LED_0603_1608Metric_dc75b572683f"
  LinkPlacement = pos=(4.7,28.175,0) rot=(0,0,-1;1.5708rad)
  LinkedObject = -> Shape004
  Placement = pos=(4.7,28.175,0) rot=(0,0,-1;1.5708rad)
FEATURE [App::Link] C15_C_0603_1608Metric_09ddd0478757_ln_018  label="C44_C_0603_1608Metric_1898ed5e7091"
  LinkPlacement = pos=(36.9,33.02,0) rot=(0,0,1;1.5708rad)
  LinkedObject = -> Shape003
  Placement = pos=(36.9,33.02,0) rot=(0,0,1;1.5708rad)
FEATURE [App::Link] R21_R_0805_2012Metric_4eff570911b6_ln_010  label="R22_R_0805_2012Metric_455d99f14320"
  LinkPlacement = pos=(34.3,26.2,0) rot=(0,0,1;0rad)
  LinkedObject = -> Shape007
  Placement = pos=(34.3,26.2,0) rot=(0,0,1;0rad)
FEATURE [App::Link] R9_R_0603_1608Metric_fe9d9f34c5f9_ln_015  label="R18_R_0603_1608Metric_e5275256b3fe"
  LinkPlacement = pos=(22.7,13.246,0) rot=(0,0,-1;1.5708rad)
  LinkedObject = -> Shape002
  Placement = pos=(22.7,13.246,0) rot=(0,0,-1;1.5708rad)
FEATURE [App::Link] U3_SOT_23_5_e32904241429_ln_001  label="U1_SOT_23_5_8fc5e1a9f18e"
  LinkPlacement = pos=(34.37,83.0215,0) rot=(0,0,1;0rad)
  LinkedObject = -> Shape008
  Placement = pos=(34.37,83.0215,0) rot=(0,0,1;0rad)
FEATURE [App::Part] Top_ed05
  Group = -> [Shape,Shape001,Shape002,D6_D_SOD_123_86f777a7cf57_ln_,Shape003,C15_C_0603_1608Metric_09ddd0478757_ln_,Shape004,Shape005,R9_R_0603_1608Metric_fe9d9f34c5f9_ln_,C15_C_0603_1608Metric_09ddd0478757_ln_001,CAS_120B1,R9_R_0603_1608Metric_fe9d9f34c5f9_ln_001,R9_R_0603_1608Metric_fe9d9f34c5f9_ln_002,C15_C_0603_1608Metric_09ddd0478757_ln_002,C38_C_0805_2012Metric_74cbd35bff10_ln_,Shape006,+74 more]
  Origin = -> Origin003
FEATURE [Part::Feature] Shape012  label="R36_R_Axial_DIN0617_L170mm_D60mm_P3048mm_Horizontal_e9082eb0809f"
  Placement = pos=(80.8,75.438,-1.6) rot=(0.707107,-0.707107,0;3.14159rad)
  shape: bbox 6.494 x 31.54 x 9.247 mm, 17 faces (baked)
FEATURE [App::Link] C38_C_0805_2012Metric_74cbd35bff10_ln_011  label="C30_C_0805_2012Metric_99b0a26469c9"
  LinkPlacement = pos=(25.8,20.7,-1.6) rot=(1,0,0;3.14159rad)
  LinkedObject = -> Shape005
  Placement = pos=(25.8,20.7,-1.6) rot=(1,0,0;3.14159rad)
FEATURE [App::Link] C15_C_0603_1608Metric_09ddd0478757_ln_019  label="C10_C_0603_1608Metric_a9055c7e1f35"
  LinkPlacement = pos=(10,27.2,-1.6) rot=(0,1,0;3.14159rad)
  LinkedObject = -> Shape003
  Placement = pos=(10,27.2,-1.6) rot=(0,1,0;3.14159rad)
FEATURE [App::Link] C38_C_0805_2012Metric_74cbd35bff10_ln_012  label="C12_C_0805_2012Metric_7a36f4b334d7"
  LinkPlacement = pos=(4.7,23.5,-1.6) rot=(0.707107,0.707107,0;3.14159rad)
  LinkedObject = -> Shape005
  Placement = pos=(4.7,23.5,-1.6) rot=(0.707107,0.707107,0;3.14159rad)
FEATURE [Part::Feature] Shape013  label="J4_Broadcom_AFBR-16xxZ_Horizontal_9b6c4e7f7e3c"
  Placement = pos=(11.2,84.664,-1.6) rot=(0,1,0;3.14159rad)
  shape: bbox 17.71 x 11.7 x 11.4 mm, 100 faces (baked)
FEATURE [App::Link] R21_R_0805_2012Metric_4eff570911b6_ln_011  label="R11_R_0805_2012Metric_904fb74af206"
  LinkPlacement = pos=(23.492,38.646,-1.6) rot=(1,0,0;3.14159rad)
  LinkedObject = -> Shape007
  Placement = pos=(23.492,38.646,-1.6) rot=(1,0,0;3.14159rad)
FEATURE [Part::Feature] Part__Feature005  label="79fa9e9c-a09d-11ed-8f45-a0cec80452fd_part"
  shape: bbox 8.4 x 14.4 x 13.5 mm, 26 faces (baked)
FEATURE [App::Part] _9fa9e9c_a09d_11ed_8f45_a0cec80452fd  label="79fa9e9c-a09d-11ed-8f45-a0cec80452fd"
  Group = -> [Part__Feature005]
  Origin = -> Origin010
FEATURE [Part::Feature] Part__Feature006  label="79faa16c-a09d-11ed-8f45-a0cec80452fd_part"
  shape: bbox 1.1 x 1.1 x 2.6 mm, 12 faces (baked)
FEATURE [Part::Feature] Part__Feature007  label="79faa16c-a09d-11ed-8f45-a0cec80452fd_part001"
  shape: bbox 1.1 x 1.1 x 2.6 mm, 12 faces (baked)
FEATURE [Part::Feature] Part__Feature008  label="79faa16c-a09d-11ed-8f45-a0cec80452fd_part002"
  shape: bbox 1.1 x 1.1 x 2.6 mm, 12 faces (baked)
FEATURE [Part::Feature] Part__Feature009  label="79faa16c-a09d-11ed-8f45-a0cec80452fd_part003"
  shape: bbox 1.1 x 1.1 x 2.6 mm, 12 faces (baked)
FEATURE [App::Part] _9faa16c_a09d_11ed_8f45_a0cec80452fd_part  label="79faa16c-a09d-11ed-8f45-a0cec80452fd_part004"
  Group = -> [Part__Feature006,Part__Feature007,Part__Feature008,Part__Feature009]
  Origin = -> Origin011
FEATURE [App::Part] _9faa16c_a09d_11ed_8f45_a0cec80452fd  label="79faa16c-a09d-11ed-8f45-a0cec80452fd"
  Group = -> [_9faa16c_a09d_11ed_8f45_a0cec80452fd_part]
  Origin = -> Origin012
FEATURE [App::Part] _9fa99c4_a09d_11ed_8f45_a0cec80452fd  label="79fa99c4-a09d-11ed-8f45-a0cec80452fd"
  Group = -> [_9fa9e9c_a09d_11ed_8f45_a0cec80452fd,_9faa16c_a09d_11ed_8f45_a0cec80452fd]
  Origin = -> Origin013
FEATURE [App::Part] CQ_assembly  label="J1_CQ assembly_c40872800de1"
  Group = -> [_9fa99c4_a09d_11ed_8f45_a0cec80452fd]
  Origin = -> Origin014
  Placement = pos=(12.4,40.678,-1.6) rot=(0.707107,0.707107,0;3.14159rad)
FEATURE [Part::Feature] Shape014  label="J10_PinHeader_1x02_P254mm_Horizontal_7643f22ec726"
  Placement = pos=(24.8,74.1115,-1.6) rot=(0,1,0;3.14159rad)
  shape: bbox 10.36 x 5.08 x 5.54 mm, 58 faces (baked)
FEATURE [App::Link] C38_C_0805_2012Metric_74cbd35bff10_ln_013  label="C28_C_0805_2012Metric_76606bb4505c"
  LinkPlacement = pos=(25.8,28.232,-1.6) rot=(1,0,0;3.14159rad)
  LinkedObject = -> Shape005
  Placement = pos=(25.8,28.232,-1.6) rot=(1,0,0;3.14159rad)
FEATURE [Part::Feature] Shape015  label="J2_C-413638-E_37cd69765024[2]"
  Placement = pos=(110.98,49.92,-5.6) rot=(0.57735,-0.57735,0.57735;4.18879rad)
  shape: bbox 25.2 x 94 x 14.8 mm, 484 faces (baked)
FEATURE [App::Link] R9_R_0603_1608Metric_fe9d9f34c5f9_ln_016  label="R4_R_0603_1608Metric_d5e5e0a8c182"
  LinkPlacement = pos=(3.875,35.5,-1.6) rot=(0.707107,-0.707107,0;3.14159rad)
  LinkedObject = -> Shape002
  Placement = pos=(3.875,35.5,-1.6) rot=(0.707107,-0.707107,0;3.14159rad)
FEATURE [App::Link] R9_R_0603_1608Metric_fe9d9f34c5f9_ln_017  label="R1_R_0603_1608Metric_12d23797164c"
  LinkPlacement = pos=(4.1,9.525,-1.6) rot=(0.707107,0.707107,0;3.14159rad)
  LinkedObject = -> Shape002
  Placement = pos=(4.1,9.525,-1.6) rot=(0.707107,0.707107,0;3.14159rad)
FEATURE [App::Link] J10_PinHeader_1x02_P254mm_Horizontal_7643f22ec726_ln_  label="J11_PinHeader_1x02_P254mm_Horizontal_fc1500a1b926"
  LinkPlacement = pos=(24.8,63.9515,-1.6) rot=(0,1,0;3.14159rad)
  LinkedObject = -> Shape014
  Placement = pos=(24.8,63.9515,-1.6) rot=(0,1,0;3.14159rad)
FEATURE [Part::Feature] Shape016  label="J13_1_cfcac89c0bd5[2]"
  Placement = pos=(96.5,44.12,-1.6) rot=(0.707107,-0.707107,0;3.14159rad)
  shape: bbox 7 x 4.98 x 4.98 mm, 13 faces (baked)
FEATURE [Part::Feature] Shape017  label="R39_R_4020_10251Metric_6d765f65bd79"
  Placement = pos=(64.4,75.4,-1.6) rot=(1,0,0;3.14159rad)
  shape: bbox 10.2 x 5.1 x 0.6 mm, 26 faces (baked)
FEATURE [Part::Feature] Part__Feature010  label="T1T1M-02-T-SH-L"
  Placement = pos=(0,0,0) rot=(1,0,0;1.5708rad)
  shape: bbox 4.4 x 4.6 x 5.2 mm, 86 faces (baked)
FEATURE [Part::Feature] Part__Feature011  label="P2T1M-02-F-SH-L"
  Placement = pos=(0,0,0) rot=(1,0,0;1.5708rad)
  shape: bbox 1.2 x 2.22 x 1.2 mm, 19 faces (baked)
FEATURE [Part::Feature] Part__Feature012  label="P22T1M-02-F-SH-L"
  Placement = pos=(0,0,0) rot=(1,0,0;1.5708rad)
  shape: bbox 1.2 x 0.4 x 3.971 mm, 15 faces (baked)
FEATURE [App::Part] T1M_02_F_SH_L  label="J6_T1M-02-F-SH-L_0a7fe3b67a9c[2]"
  Group = -> [Part__Feature010,Part__Feature011,Part__Feature012]
  Origin = -> Origin015
  Placement = pos=(31.4,67.734,-3.98) rot=(0.57735,0.57735,-0.57735;4.18879rad)
FEATURE [Part::Feature] Shape018  label="HS1_sk687_9ae714bd8fdf[2]"
  Placement = pos=(33.982,3.642,-1.55) rot=(0,0.707107,-0.707107;3.14159rad)
  shape: bbox 42 x 50 x 35 mm, 258 faces (baked)
FEATURE [App::Link] J6_T1M_02_F_SH_L_0a7fe3b67a9c_2__ln_  label="J7_T1M-02-F-SH-L_7059b7eb8092[2]"
  LinkPlacement = pos=(31.4,77.894,-3.98) rot=(0.57735,0.57735,-0.57735;4.18879rad)
  LinkedObject = -> T1M_02_F_SH_L
  Placement = pos=(31.4,77.894,-3.98) rot=(0.57735,0.57735,-0.57735;4.18879rad)
FEATURE [App::Link] R39_R_4020_10251Metric_6d765f65bd79_ln_  label="R38_R_4020_10251Metric_23694b22d5d4"
  LinkPlacement = pos=(64.4,81.2,-1.6) rot=(1,0,0;3.14159rad)
  LinkedObject = -> Shape017
  Placement = pos=(64.4,81.2,-1.6) rot=(1,0,0;3.14159rad)
FEATURE [App::Link] C38_C_0805_2012Metric_74cbd35bff10_ln_014  label="C13_C_0805_2012Metric_5e4ca477a655"
  LinkPlacement = pos=(9.9,21.7,-1.6) rot=(1,0,0;3.14159rad)
  LinkedObject = -> Shape005
  Placement = pos=(9.9,21.7,-1.6) rot=(1,0,0;3.14159rad)
FEATURE [App::Link] J10_PinHeader_1x02_P254mm_Horizontal_7643f22ec726_ln_001  label="J9_PinHeader_1x02_P254mm_Horizontal_9237b5c6f450"
  LinkPlacement = pos=(24.8,84.2715,-1.6) rot=(0,1,0;3.14159rad)
  LinkedObject = -> Shape014
  Placement = pos=(24.8,84.2715,-1.6) rot=(0,1,0;3.14159rad)
FEATURE [App::Link] R9_R_0603_1608Metric_fe9d9f34c5f9_ln_018  label="R5_R_0603_1608Metric_697492a11508"
  LinkPlacement = pos=(3.875,31.775,-1.6) rot=(0.707107,-0.707107,0;3.14159rad)
  LinkedObject = -> Shape002
  Placement = pos=(3.875,31.775,-1.6) rot=(0.707107,-0.707107,0;3.14159rad)
FEATURE [App::Link] J4_Broadcom_AFBR_16xxZ_Horizontal_9b6c4e7f7e3c_ln_  label="J5_Broadcom_AFBR-16xxZ_Horizontal_cc90251d43e9"
  LinkPlacement = pos=(11.2,64.344,-1.6) rot=(0,1,0;3.14159rad)
  LinkedObject = -> Shape013
  Placement = pos=(11.2,64.344,-1.6) rot=(0,1,0;3.14159rad)
FEATURE [App::Link] C15_C_0603_1608Metric_09ddd0478757_ln_020  label="C9_C_0603_1608Metric_8758c5b1e71b"
  LinkPlacement = pos=(10,28.7,-1.6) rot=(0,1,0;3.14159rad)
  LinkedObject = -> Shape003
  Placement = pos=(10,28.7,-1.6) rot=(0,1,0;3.14159rad)
FEATURE [App::Link] R9_R_0603_1608Metric_fe9d9f34c5f9_ln_019  label="R7_R_0603_1608Metric_6e0015b41d89"
  LinkPlacement = pos=(2.9,24.5,-1.6) rot=(0.707107,-0.707107,0;3.14159rad)
  LinkedObject = -> Shape002
  Placement = pos=(2.9,24.5,-1.6) rot=(0.707107,-0.707107,0;3.14159rad)
FEATURE [Part::Feature] Part__Feature013  label="CFP_RB4_42X40X20_L43H41T21S37.5S110.2LL4F1.25"
  shape: bbox 43 x 45 x 21 mm, 30 faces (baked)
FEATURE [Part::Feature] Part__Feature014  label="CFP_RB4_42X40X20_L43H41T21S37.5S110.2LL4F1.026"
  shape: bbox 8.475 x 4.477 x 0.005 mm, 19 faces (baked)
FEATURE [Part::Feature] Part__Feature015  label="CFP_RB4_42X40X20_L43H41T21S37.5S110.2LL4F1.027"
  shape: bbox 10.33 x 4.477 x 0.005 mm, 25 faces (baked)
FEATURE [Part::Feature] Part__Feature016  label="CFP_RB4_42X40X20_L43H41T21S37.5S110.2LL4F1.028"
  shape: bbox 5.39 x 4.477 x 0.005 mm, 13 faces (baked)
FEATURE [App::Part] CFP_RB4_42X40X20_L43H41T21S37_5S110_2LL4F1_25  label="C1_CFP_RB4_42X40X20_L43H41T21S37.5S110.2LL4F1.029_59f146c23d11[2]"
  Group = -> [Part__Feature013,Part__Feature014,Part__Feature015,Part__Feature016]
  Origin = -> Origin016
  Placement = pos=(56.028,56.336,-1.6) rot=(0.57735,-0.57735,0.57735;4.18879rad)
FEATURE [Part::Feature] Shape019  label="Q1_TO-247-4_Vertical_4070ae466a86"
  Placement = pos=(40.55,42.209,-1.6) rot=(0.707107,-0.707107,0;3.14159rad)
  shape: bbox 5.03 x 15.9 x 41.1 mm, 74 faces (baked)
FEATURE [App::Link] J13_1_cfcac89c0bd5_2__ln_  label="J14_1_45c35c22a121[2]"
  LinkPlacement = pos=(96.5,64.44,-1.6) rot=(0.707107,-0.707107,0;3.14159rad)
  LinkedObject = -> Shape016
  Placement = pos=(96.5,64.44,-1.6) rot=(0.707107,-0.707107,0;3.14159rad)
FEATURE [Part::Feature] Part__Feature017  label="RKZ-xx2005D_case"
  shape: bbox 19.65 x 10.2 x 7.05 mm, 112 faces (baked)
FEATURE [Part::Feature] Part__Feature018  label="RKZ-xx2005D_pin1(+Vin)"
  shape: bbox 0.5 x 4.6 x 0.25 mm, 6 faces (baked)
FEATURE [Part::Feature] Part__Feature019  label="RKZ-xx2005D_pin7(+Vout)"
  shape: bbox 0.5 x 4.6 x 0.25 mm, 6 faces (baked)
FEATURE [Part::Feature] Part__Feature020  label="RKZ-xx2005D_pin5(-Vout)"
  shape: bbox 0.5 x 4.6 x 0.25 mm, 6 faces (baked)
FEATURE [Part::Feature] Part__Feature021  label="RKZ-xx2005D_pin6(Com)"
  shape: bbox 0.5 x 4.6 x 0.25 mm, 6 faces (baked)
FEATURE [Part::Feature] Part__Feature022  label="RKZ-xx2005D_pin2(-Vin)"
  shape: bbox 0.5 x 4.6 x 0.25 mm, 6 faces (baked)
FEATURE [Part::Feature] Part__Feature023  label="RKZ-xx2005D_potting"
  shape: bbox 18.55 x 8.95 x 6 mm, 6 faces (baked)
FEATURE [App::Part] RKZ_xx2005D  label="U6_RKZ_xx2005D_0645041a10aa[2]"
  Group = -> [Part__Feature017,Part__Feature018,Part__Feature019,Part__Feature020,Part__Feature021,Part__Feature022,Part__Feature023]
  Origin = -> Origin017
  Placement = pos=(18.85,12.664,-1.6) rot=(-1,0,0;1.5708rad)
FEATURE [App::Link] U6_RKZ_xx2005D_0645041a10aa_2__ln_  label="U4_RKZ_xx2005D_740929d25b34[2]"
  LinkPlacement = pos=(18.85,33.276,-1.6) rot=(-1,0,0;1.5708rad)
  LinkedObject = -> RKZ_xx2005D
  Placement = pos=(18.85,33.276,-1.6) rot=(-1,0,0;1.5708rad)
FEATURE [App::Link] J6_T1M_02_F_SH_L_0a7fe3b67a9c_2__ln_001  label="J8_T1M-02-F-SH-L_f87a2e85d4db[2]"
  LinkPlacement = pos=(31.4,57.574,-3.98) rot=(0.57735,0.57735,-0.57735;4.18879rad)
  LinkedObject = -> T1M_02_F_SH_L
  Placement = pos=(31.4,57.574,-3.98) rot=(0.57735,0.57735,-0.57735;4.18879rad)
FEATURE [App::Link] Q1_TO_247_4_Vertical_4070ae466a86_ln_  label="Q2_TO-247-4_Vertical_c7c841d41241"
  LinkPlacement = pos=(40.55,25.209,-1.6) rot=(0.707107,-0.707107,0;3.14159rad)
  LinkedObject = -> Shape019
  Placement = pos=(40.55,25.209,-1.6) rot=(0.707107,-0.707107,0;3.14159rad)
FEATURE [App::Link] C38_C_0805_2012Metric_74cbd35bff10_ln_015  label="C29_C_0805_2012Metric_ea01a7009c54"
  LinkPlacement = pos=(25.7995,25.692,-1.6) rot=(0,1,0;3.14159rad)
  LinkedObject = -> Shape005
  Placement = pos=(25.7995,25.692,-1.6) rot=(0,1,0;3.14159rad)
FEATURE [App::Link] L5_L_0603_1608Metric_90973c27a168_ln_004  label="L1_L_0603_1608Metric_e9d47b7cc21e"
  LinkPlacement = pos=(7.375,23.5,-1.6) rot=(1,0,0;3.14159rad)
  LinkedObject = -> Shape011
  Placement = pos=(7.375,23.5,-1.6) rot=(1,0,0;3.14159rad)
FEATURE [App::Link] R21_R_0805_2012Metric_4eff570911b6_ln_012  label="R12_R_0805_2012Metric_000eced81897"
  LinkPlacement = pos=(24.892,7.874,-1.6) rot=(1,0,0;3.14159rad)
  LinkedObject = -> Shape007
  Placement = pos=(24.892,7.874,-1.6) rot=(1,0,0;3.14159rad)
FEATURE [App::Link] R9_R_0603_1608Metric_fe9d9f34c5f9_ln_020  label="R6_R_0603_1608Metric_4e81408e4251"
  LinkPlacement = pos=(3.9,28.175,-1.6) rot=(0.707107,-0.707107,0;3.14159rad)
  LinkedObject = -> Shape002
  Placement = pos=(3.9,28.175,-1.6) rot=(0.707107,-0.707107,0;3.14159rad)
FEATURE [App::Link] R36_R_Axial_DIN0617_L170mm_D60mm_P3048mm_Horizontal_e9082eb0809f_ln_  label="R37_R_Axial_DIN0617_L170mm_D60mm_P3048mm_Horizontal_4fcf1ba42225"
  LinkPlacement = pos=(80.8,41.91,-1.6) rot=(0.707107,-0.707107,0;3.14159rad)
  LinkedObject = -> Shape012
  Placement = pos=(80.8,41.91,-1.6) rot=(0.707107,-0.707107,0;3.14159rad)
FEATURE [App::Link] J13_1_cfcac89c0bd5_2__ln_001  label="J12_1_5d39db0f3e7c[2]"
  LinkPlacement = pos=(96.5,23.8,-1.6) rot=(0.707107,-0.707107,0;3.14159rad)
  LinkedObject = -> Shape016
  Placement = pos=(96.5,23.8,-1.6) rot=(0.707107,-0.707107,0;3.14159rad)
FEATURE [App::Link] J13_1_cfcac89c0bd5_2__ln_002  label="J15_1_77f750f6aa21[2]"
  LinkPlacement = pos=(96.5,84.76,-1.6) rot=(0.707107,-0.707107,0;3.14159rad)
  LinkedObject = -> Shape016
  Placement = pos=(96.5,84.76,-1.6) rot=(0.707107,-0.707107,0;3.14159rad)
FEATURE [App::Link] C38_C_0805_2012Metric_74cbd35bff10_ln_016  label="C31_C_0805_2012Metric_a2a63c8358cd"
  LinkPlacement = pos=(25.8,18.7,-1.6) rot=(0,1,0;3.14159rad)
  LinkedObject = -> Shape005
  Placement = pos=(25.8,18.7,-1.6) rot=(0,1,0;3.14159rad)
FEATURE [Part::Feature] Shape020  label="D7_D_SMC_a35920f9d814"
  Placement = pos=(20.55,23.216,-1.6) rot=(0.707107,-0.707107,0;3.14159rad)
  shape: bbox 5.9 x 8 x 2.31 mm, 41 faces (baked)
FEATURE [App::Link] J4_Broadcom_AFBR_16xxZ_Horizontal_9b6c4e7f7e3c_ln_001  label="J3_Broadcom_AFBR-16xxZ_Horizontal_92a701fb3616"
  LinkPlacement = pos=(11.2,74.504,-1.6) rot=(0,1,0;3.14159rad)
  LinkedObject = -> Shape013
  Placement = pos=(11.2,74.504,-1.6) rot=(0,1,0;3.14159rad)
FEATURE [App::Part] Bot_ed05
  Group = -> [Shape012,C38_C_0805_2012Metric_74cbd35bff10_ln_011,C15_C_0603_1608Metric_09ddd0478757_ln_019,C38_C_0805_2012Metric_74cbd35bff10_ln_012,Shape013,R21_R_0805_2012Metric_4eff570911b6_ln_011,CQ_assembly,Shape014,C38_C_0805_2012Metric_74cbd35bff10_ln_013,Shape015,R9_R_0603_1608Metric_fe9d9f34c5f9_ln_016,R9_R_0603_1608Metric_fe9d9f34c5f9_ln_017,J10_PinHeader_1x02_P254mm_Horizontal_7643f22ec726_ln_,+29 more]
  Origin = -> Origin004
FEATURE [App::Part] Step_Models_ed05
  Group = -> [Top_ed05,Bot_ed05]
  Origin = -> Origin002
FEATURE [App::Part] Board_ed05  label="HalfBridge_SiC"
  Group = -> [Local_CS_ed05,Board_Geoms_ed05,Step_Models_ed05]
  Origin = -> Origin001
